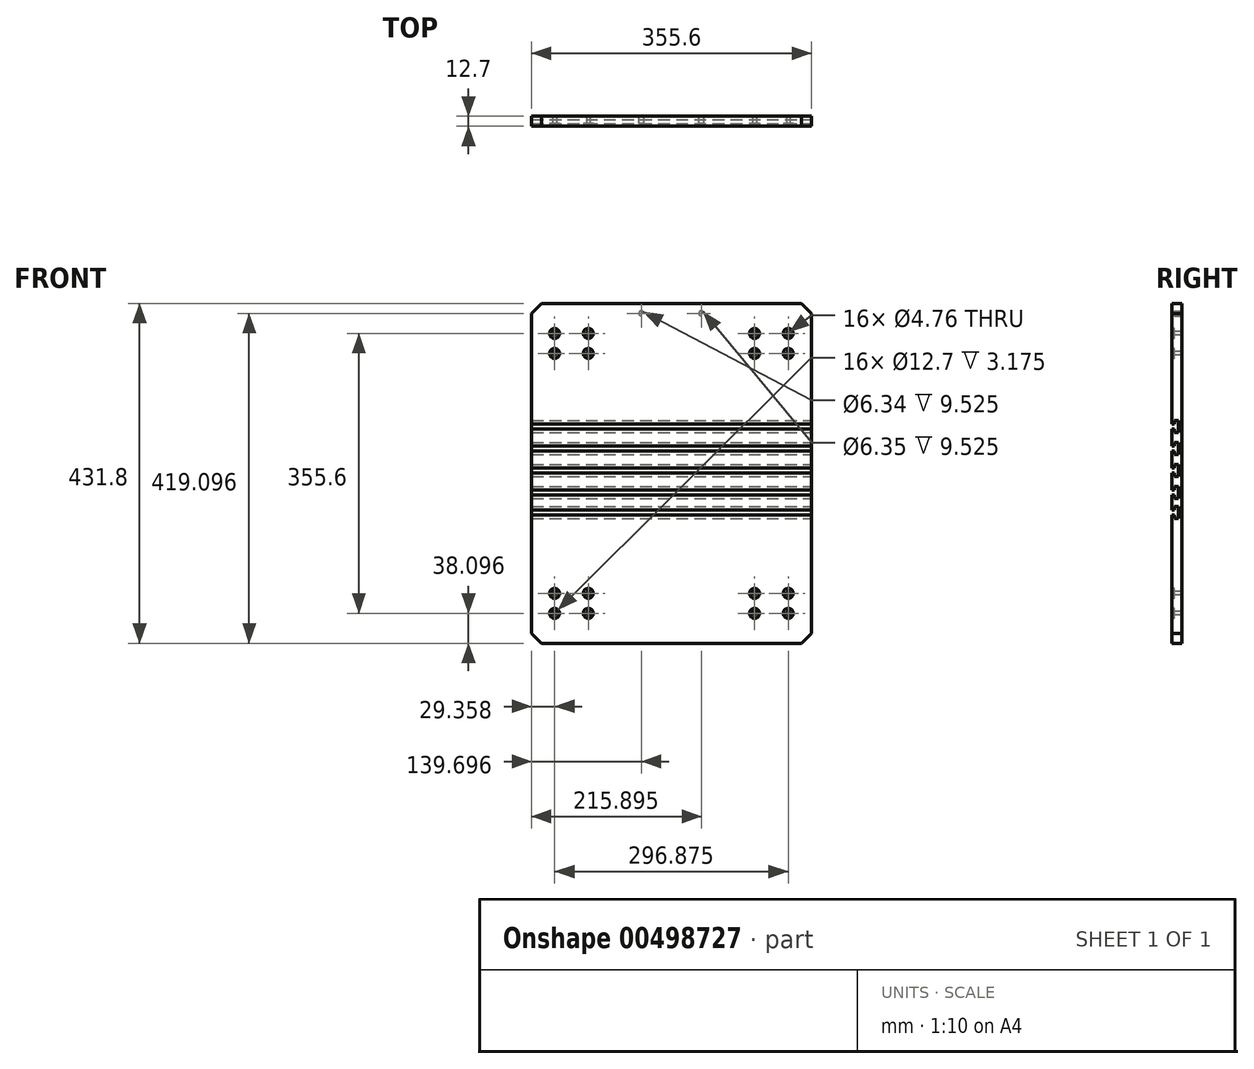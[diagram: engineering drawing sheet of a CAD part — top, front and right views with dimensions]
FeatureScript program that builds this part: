
annotation { "Feature Type Name" : "Feature", "Feature Type Description" : "" }
export const myFeature = defineFeature(function(context is Context, id is Id, definition is map)
    precondition{}
    {
        {
            var Q0;
            Q0=qCreatedBy(makeId("Front.planeOp"),FACE);
            var sketch = newSketch(context, id + "F0", { "sketchPlane" : qUnion([Q0])});
            skLineSegment(sketch, "E0.bottom", {"start": v(-66.48, -50.86) * mm, "end": v(289.12, -50.86) * mm});
            skLineSegment(sketch, "E0.top", {"start": v(-66.48, 380.94) * mm, "end": v(289.12, 380.94) * mm});
            skLineSegment(sketch, "E0.left", {"start": v(-66.48, -50.86) * mm, "end": v(-66.48, 380.94) * mm});
            skLineSegment(sketch, "E0.right", {"start": v(289.12, -50.86) * mm, "end": v(289.12, 380.94) * mm});
            skSolve(sketch);
        }
        {
            var Q0;
            Q0=qSketchRegion(id+"F0",true);
            extrude(context, id + "F1", {"entities" : qUnion([Q0]), "depth" : 12.7 * mm});
        }
        {
            var Q0;
            Q0=makeQuery(id+"F1.opExtrude","SWEPT_EDGE",EDGE,{"disambiguationData":[OSD([sQuery(id+"F0.wireOp",EDGE,"E0.top"),sQuery(id+"F0.wireOp",EDGE,"E0.left")])]});
            var Q1;
            Q1=makeQuery(id+"F1.opExtrude","SWEPT_EDGE",EDGE,{"disambiguationData":[OSD([sQuery(id+"F0.wireOp",EDGE,"E0.top"),sQuery(id+"F0.wireOp",EDGE,"E0.right")])]});
            var Q2;
            Q2=makeQuery(id+"F1.opExtrude","SWEPT_EDGE",EDGE,{"disambiguationData":[OSD([sQuery(id+"F0.wireOp",EDGE,"E0.bottom"),sQuery(id+"F0.wireOp",EDGE,"E0.right")])]});
            var Q3;
            Q3=makeQuery(id+"F1.opExtrude","SWEPT_EDGE",EDGE,{"disambiguationData":[OSD([sQuery(id+"F0.wireOp",EDGE,"E0.bottom"),sQuery(id+"F0.wireOp",EDGE,"E0.left")])]});
            chamfer(context, id + "F2", {"entities" : qUnion([Q0, Q1, Q2, Q3]), "chamferType" : ChamferType.OFFSET_ANGLE, "width" : 12.7 * mm, "oppositeDirection" : false, "angle" : 45 * degree, "tangentPropagation" : true});
        }
        {
            var Q0;
            Q0=makeQuery(id+"F1.opExtrude","CAP_FACE",FACE,{"disambiguationData":[OSD([sQuery(id+"F0.wireOp",EDGE,"E0.bottom"),sQuery(id+"F0.wireOp",EDGE,"E0.top"),sQuery(id+"F0.wireOp",EDGE,"E0.left"),sQuery(id+"F0.wireOp",EDGE,"E0.right")])],"isStart":false});
            var sketch = newSketch(context, id + "F3", { "sketchPlane" : qUnion([Q0])});
            skCircle(sketch, "E1", {"center": v(-37.12, 317.44) * mm, "radius": 4.76 * mm});
            skCircle(sketch, "E2", {"center": v(-37.12, -12.76) * mm, "radius": 4.76 * mm});
            skCircle(sketch, "E3", {"center": v(5.75, 317.44) * mm, "radius": 4.76 * mm});
            skCircle(sketch, "E4", {"center": v(5.75, 342.84) * mm, "radius": 4.76 * mm});
            skCircle(sketch, "E5", {"center": v(-37.12, 342.84) * mm, "radius": 4.76 * mm});
            skCircle(sketch, "E6", {"center": v(-37.12, 12.64) * mm, "radius": 4.76 * mm});
            skCircle(sketch, "E7", {"center": v(5.75, -12.76) * mm, "radius": 4.76 * mm});
            skCircle(sketch, "E8", {"center": v(216.88, 342.84) * mm, "radius": 4.76 * mm});
            skCircle(sketch, "E9", {"center": v(259.75, 12.64) * mm, "radius": 4.76 * mm});
            skCircle(sketch, "E10", {"center": v(259.75, 317.44) * mm, "radius": 4.76 * mm});
            skCircle(sketch, "E11", {"center": v(259.75, 342.84) * mm, "radius": 4.76 * mm});
            skCircle(sketch, "E12", {"center": v(259.75, -12.76) * mm, "radius": 4.76 * mm});
            skCircle(sketch, "E13", {"center": v(216.88, 317.44) * mm, "radius": 4.76 * mm});
            skCircle(sketch, "E14", {"center": v(216.88, -12.76) * mm, "radius": 4.76 * mm});
            skCircle(sketch, "E15", {"center": v(216.88, 12.64) * mm, "radius": 4.76 * mm});
            skCircle(sketch, "E16", {"center": v(5.75, 12.64) * mm, "radius": 4.76 * mm});
            skCircle(sketch, "E17", {"center": v(73.22, 368.24) * mm, "radius": 3.18 * mm});
            skCircle(sketch, "E18", {"center": v(149.42, 368.24) * mm, "radius": 3.18 * mm});
            skCircle(sketch, "E19", {"center": v(149.42, -38.16) * mm, "radius": 3.18 * mm});
            skCircle(sketch, "E20", {"center": v(73.22, -38.16) * mm, "radius": 3.18 * mm});
            skSolve(sketch);
        }
        {
            var Q0;
            Q0=sQuery(id+"F3.wireOp",VERTEX,"E5.center");
            var Q1;
            Q1=sQuery(id+"F3.wireOp",VERTEX,"E1.center");
            var Q2;
            Q2=sQuery(id+"F3.wireOp",VERTEX,"E3.center");
            var Q3;
            Q3=sQuery(id+"F3.wireOp",VERTEX,"E4.center");
            var Q4;
            Q4=sQuery(id+"F3.wireOp",VERTEX,"E13.center");
            var Q5;
            Q5=sQuery(id+"F3.wireOp",VERTEX,"E8.center");
            var Q6;
            Q6=sQuery(id+"F3.wireOp",VERTEX,"E10.center");
            var Q7;
            Q7=sQuery(id+"F3.wireOp",VERTEX,"E11.center");
            var Q8;
            Q8=sQuery(id+"F3.wireOp",VERTEX,"E12.center");
            var Q9;
            Q9=sQuery(id+"F3.wireOp",VERTEX,"E9.center");
            var Q10;
            Q10=sQuery(id+"F3.wireOp",VERTEX,"E14.center");
            var Q11;
            Q11=sQuery(id+"F3.wireOp",VERTEX,"E15.center");
            var Q12;
            Q12=sQuery(id+"F3.wireOp",VERTEX,"E7.center");
            var Q13;
            Q13=sQuery(id+"F3.wireOp",VERTEX,"E16.center");
            var Q14;
            Q14=sQuery(id+"F3.wireOp",VERTEX,"E2.center");
            var Q15;
            Q15=sQuery(id+"F3.wireOp",VERTEX,"E6.center");
            var Q16;
            Q16=makeQuery(id+"F1.opExtrude","SWEPT_BODY",BODY,{"disambiguationData":[OSD([sQuery(id+"F0.wireOp",EDGE,"E0.bottom"),sQuery(id+"F0.wireOp",EDGE,"E0.top"),sQuery(id+"F0.wireOp",EDGE,"E0.left"),sQuery(id+"F0.wireOp",EDGE,"E0.right")])]});
            hole(context, id + "F4", {"style" : HoleStyle.C_BORE, "endStyle" : HoleEndStyle.BLIND, "holeDiameter" : 4.76 * mm, "cBoreDiameter" : 12.7 * mm, "cBoreDepth" : 3.17 * mm, "holeDepth" : 76.2 * mm, "tappedDepth" : 12.7 * mm, "tapClearance" : 3, "startFromSketch" : true, "locations" : qUnion([Q0, Q1, Q2, Q3, Q4, Q5, Q6, Q7, Q8, Q9, Q10, Q11, Q12, Q13, Q14, Q15]), "scope" : qUnion([Q16])});
        }
        {
            var Q0;
            Q0=makeQuery(id+"F1.opExtrude","SWEPT_FACE",FACE,{"disambiguationData":[OSD([sQuery(id+"F0.wireOp",EDGE,"E0.right")])]});
            var sketch = newSketch(context, id + "F5", { "sketchPlane" : qUnion([Q0])});
            skSolve(sketch);
        }
        {
            var Q0;
            {var subQ0=sQuery(id+"F0.wireOp",EDGE,"E0.right");Q0=makeQuery(id+"F5.imprint","IMPRINT",FACE,{"disambiguationData":[TD([[makeQuery(id+"F5.imprint","IMPRINT",EDGE,{"derivedFrom":makeQuery(id+"F1.opExtrude","CAP_EDGE",EDGE,{"disambiguationData":[OSD([subQ0])],"isStart":true})}),1.0]])]});}
            var sketch = newSketch(context, id + "F6", { "sketchPlane" : qUnion([Q0])});
            skLineSegment(sketch, "E21", {"start": v(-12.7, 165.67) * mm, "end": v(-12.7, 172.02) * mm});
            skLineSegment(sketch, "E22", {"start": v(-12.7, 165.67) * mm, "end": v(-9.53, 165.67) * mm});
            skLineSegment(sketch, "E23", {"start": v(-12.7, 172.02) * mm, "end": v(-9.53, 172.02) * mm});
            skLineSegment(sketch, "E24", {"start": v(-9.53, 172.02) * mm, "end": v(-9.53, 176.47) * mm});
            skLineSegment(sketch, "E25", {"start": v(-9.53, 176.47) * mm, "end": v(-4.45, 176.47) * mm});
            skLineSegment(sketch, "E26", {"start": v(-4.45, 176.47) * mm, "end": v(-4.45, 161.23) * mm});
            skLineSegment(sketch, "E27", {"start": v(-4.45, 161.23) * mm, "end": v(-9.52, 161.23) * mm});
            skLineSegment(sketch, "E28", {"start": v(-9.52, 161.23) * mm, "end": v(-9.53, 165.67) * mm});
            skLineSegment(sketch, "E29", {"start": v(-12.7, 182.82) * mm, "end": v(0, 182.82) * mm, "construction": true});
            skLineSegment(sketch, "E30.MirrorCS", {"start": v(-12.7, 193.61) * mm, "end": v(-9.53, 193.61) * mm});
            skLineSegment(sketch, "E31.MirrorCS", {"start": v(-12.7, 199.96) * mm, "end": v(-12.7, 193.61) * mm});
            skLineSegment(sketch, "E32.MirrorCS", {"start": v(-12.7, 199.96) * mm, "end": v(-9.53, 199.96) * mm});
            skLineSegment(sketch, "E33.MirrorCS", {"start": v(-9.52, 204.4) * mm, "end": v(-9.53, 199.96) * mm});
            skLineSegment(sketch, "E34.MirrorCS", {"start": v(-4.45, 204.4) * mm, "end": v(-9.52, 204.4) * mm});
            skLineSegment(sketch, "E35.MirrorCS", {"start": v(-4.45, 189.17) * mm, "end": v(-4.45, 204.4) * mm});
            skLineSegment(sketch, "E36.MirrorCS", {"start": v(-9.53, 189.17) * mm, "end": v(-4.45, 189.17) * mm});
            skLineSegment(sketch, "E37.MirrorCS", {"start": v(-9.53, 193.61) * mm, "end": v(-9.53, 189.17) * mm});
            skLineSegment(sketch, "E38", {"start": v(-12.7, 210.76) * mm, "end": v(0, 210.76) * mm, "construction": true});
            skLineSegment(sketch, "E39.MirrorCS", {"start": v(-4.45, 217.1) * mm, "end": v(-9.52, 217.1) * mm});
            skLineSegment(sketch, "E40.MirrorCS", {"start": v(-9.52, 217.1) * mm, "end": v(-9.53, 221.55) * mm});
            skLineSegment(sketch, "E41.MirrorCS", {"start": v(-4.44, 232.35) * mm, "end": v(-4.44, 217.1) * mm});
            skLineSegment(sketch, "E42.MirrorCS", {"start": v(-9.53, 232.35) * mm, "end": v(-4.45, 232.35) * mm});
            skLineSegment(sketch, "E43.MirrorCS", {"start": v(-9.52, 227.9) * mm, "end": v(-9.52, 232.35) * mm});
            skLineSegment(sketch, "E44.MirrorCS", {"start": v(-12.7, 227.9) * mm, "end": v(-9.53, 227.9) * mm});
            skLineSegment(sketch, "E45.MirrorCS", {"start": v(-12.7, 221.55) * mm, "end": v(-12.7, 227.9) * mm});
            skLineSegment(sketch, "E46", {"start": v(-9.53, 221.55) * mm, "end": v(-12.7, 221.55) * mm});
            skLineSegment(sketch, "E47", {"start": v(-12.7, 154.88) * mm, "end": v(0, 154.88) * mm, "construction": true});
            skLineSegment(sketch, "E48.MirrorCS", {"start": v(-4.45, 148.53) * mm, "end": v(-9.52, 148.53) * mm});
            skLineSegment(sketch, "E49.MirrorCS", {"start": v(-9.52, 148.53) * mm, "end": v(-9.53, 144.08) * mm});
            skLineSegment(sketch, "E50.MirrorCS", {"start": v(-4.45, 133.29) * mm, "end": v(-4.45, 148.53) * mm});
            skLineSegment(sketch, "E51.MirrorCS", {"start": v(-9.53, 133.29) * mm, "end": v(-4.45, 133.29) * mm});
            skLineSegment(sketch, "E52.MirrorCS", {"start": v(-9.53, 137.73) * mm, "end": v(-9.53, 133.29) * mm});
            skLineSegment(sketch, "E53.MirrorCS", {"start": v(-12.7, 137.73) * mm, "end": v(-9.53, 137.73) * mm});
            skLineSegment(sketch, "E54.MirrorCS", {"start": v(-12.7, 144.08) * mm, "end": v(-12.7, 137.73) * mm});
            skLineSegment(sketch, "E55.MirrorCS", {"start": v(-12.7, 144.08) * mm, "end": v(-9.53, 144.08) * mm});
            skLineSegment(sketch, "E56", {"start": v(-12.7, 128.2) * mm, "end": v(0, 128.2) * mm, "construction": true});
            skLineSegment(sketch, "E57.MirrorCS", {"start": v(-9.53, 118.68) * mm, "end": v(-9.53, 123.13) * mm});
            skLineSegment(sketch, "E58.MirrorCS", {"start": v(-12.7, 118.68) * mm, "end": v(-9.53, 118.68) * mm});
            skLineSegment(sketch, "E59.MirrorCS", {"start": v(-12.7, 112.33) * mm, "end": v(-12.7, 118.68) * mm});
            skLineSegment(sketch, "E60.MirrorCS", {"start": v(-12.7, 112.33) * mm, "end": v(-9.53, 112.33) * mm});
            skLineSegment(sketch, "E61.MirrorCS", {"start": v(-9.52, 107.89) * mm, "end": v(-9.53, 112.33) * mm});
            skLineSegment(sketch, "E62.MirrorCS", {"start": v(-4.45, 107.89) * mm, "end": v(-9.52, 107.89) * mm});
            skLineSegment(sketch, "E63.MirrorCS", {"start": v(-4.45, 123.13) * mm, "end": v(-4.45, 107.89) * mm});
            skLineSegment(sketch, "E64.MirrorCS", {"start": v(-9.53, 123.13) * mm, "end": v(-4.45, 123.13) * mm});
            skSolve(sketch);
        }
        {
            var Q0;
            Q0=qSketchRegion(id+"F6",true);
            extrude(context, id + "F7", {"entities" : qUnion([Q0]), "operationType" : NewBodyOperationType.REMOVE, "oppositeDirection" : true, "depth" : 355.6 * mm});
        }
        {
            var Q0;
            Q0=makeQuery(id+"F0.imprint","IMPRINT",FACE,{"disambiguationData":[TD([[makeQuery(id+"F0.imprint","IMPRINT",EDGE,{"derivedFrom":sQuery(id+"F0.wireOp",EDGE,"E0.bottom")}),1.0]])]});
            var sketch = newSketch(context, id + "F8", { "sketchPlane" : qUnion([Q0])});
            skCircle(sketch, "E65", {"center": v(149.42, 368.24) * mm, "radius": 3.18 * mm});
            skCircle(sketch, "E66", {"center": v(73.22, 368.24) * mm, "radius": 3.17 * mm});
            skSolve(sketch);
        }
        {
            var Q0;
            Q0=qSketchRegion(id+"F8",true);
            extrude(context, id + "F9", {"entities" : qUnion([Q0]), "operationType" : NewBodyOperationType.REMOVE, "depth" : 9.52 * mm});
        }
    });
